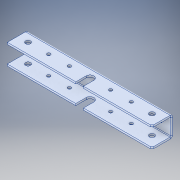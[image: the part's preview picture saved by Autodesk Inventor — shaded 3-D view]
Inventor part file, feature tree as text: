
AUTODESK INVENTOR PART (.ipt)
format: ipt  version: 2017 (Build 210142000, 142)  size: 279,552 bytes
history: native  units: in
note: dims shown in document units (in); Inventor stores cm internally (conversion verified against a paired STEP export)
features: sketch x3, hole x2, split x1, extrude x1, other x1
ambient origin geometry x8: Origin, YZ Plane, XZ Plane, XY Plane, X Axis, Y Axis, Z Axis, Center Point
bodies: Solid1 (feature_tree)
feature tree (8):
  split  "Split1"
  hole  "Hole1"  [1 undecoded]
  sketch  "Sketch3"  dims[d19=1.0in d20=0.0in d21=0.375in d22=0.75in d23=0.375in d24=0.25in d25=0.5635in d26=1.0in d27=0.8108in]
  extrude  "Extrusion2"  Depth=0.375in
  hole  "Hole3"  [1 undecoded]
  sketch  "Sketch1"  dims[d0=0.25in d1=0.25in]
  sketch  "Sketch2"  dims[d2=0.25in d3=0.75in d4=0.375in d5=0.25in d6=0.5635in d7=1.0in d8=0.8108in d9=0.375in]
  other  "Break-Corner1"
note: 2 required parameter values undecoded (feature->parameter linkage not recoverable at this tier; creation-order binding heuristic only, values carry confidence <= 0.55)
